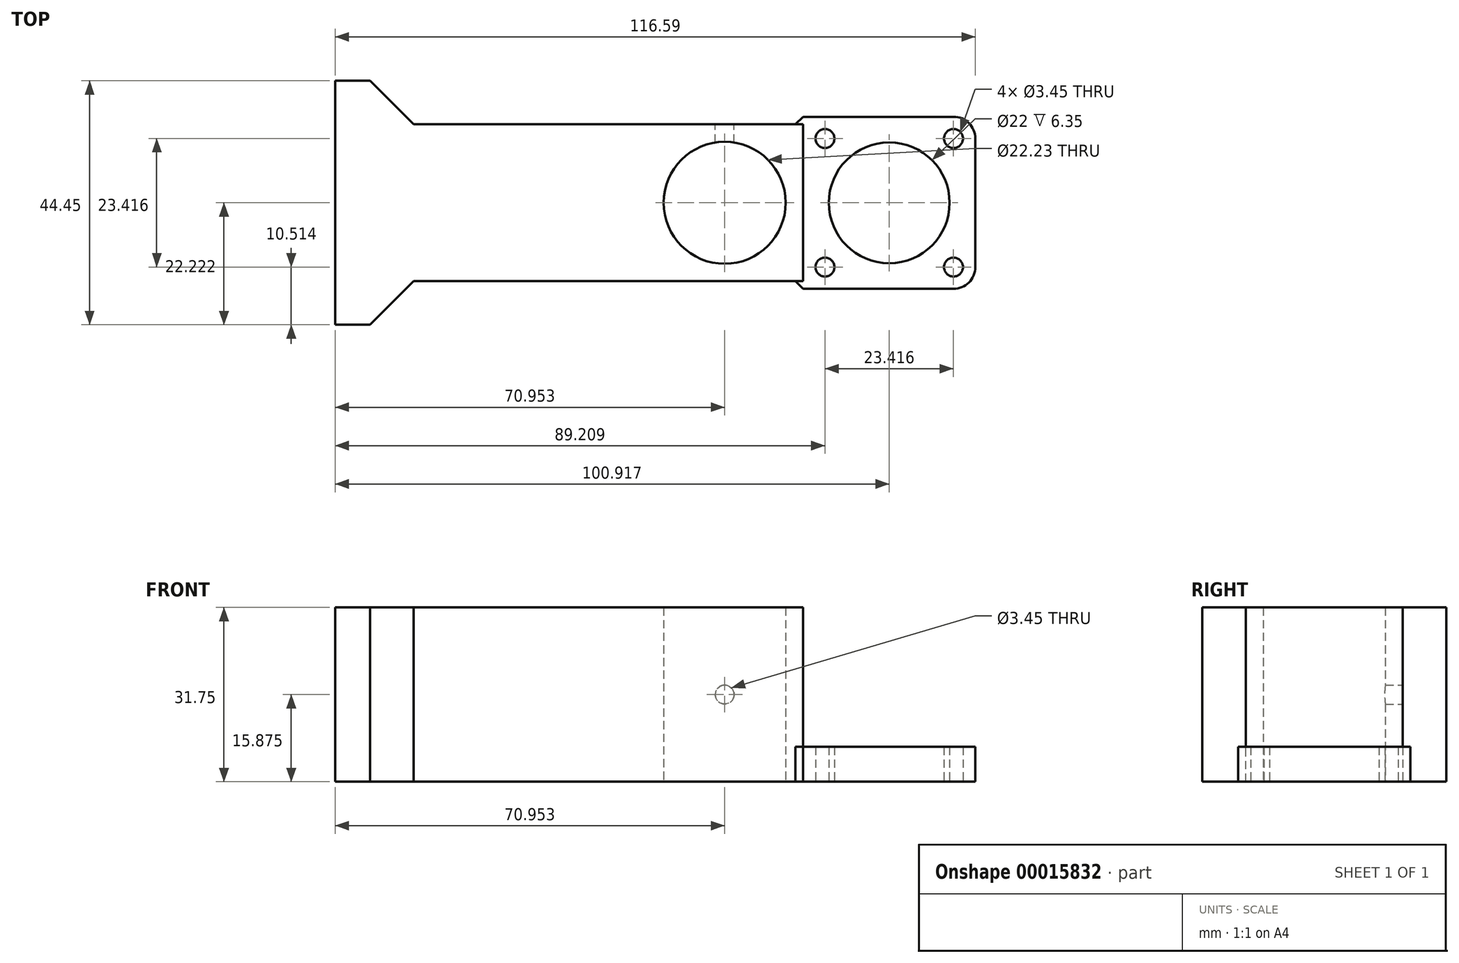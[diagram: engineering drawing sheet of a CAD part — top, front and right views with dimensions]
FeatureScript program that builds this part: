
annotation { "Feature Type Name" : "Feature", "Feature Type Description" : "" }
export const myFeature = defineFeature(function(context is Context, id is Id, definition is map)
    precondition{}
    {
        {
            var Q0;
            Q0=qCreatedBy(makeId("Top.planeOp"),FACE);
            var sketch = newSketch(context, id + "F0", { "sketchPlane" : qUnion([Q0])});
            skLineSegment(sketch, "E0.bottom", {"start": v(0, 0) * mm, "end": v(-78.9, 0) * mm});
            skLineSegment(sketch, "E0.top", {"start": v(0, -28.58) * mm, "end": v(-78.9, -28.58) * mm});
            skCircle(sketch, "E1", {"center": v(-14.29, -14.29) * mm, "radius": 11.11 * mm});
            skLineSegment(sketch, "E2", {"start": v(-14.29, -14.29) * mm, "end": v(-85.24, -14.29) * mm});
            skLineSegment(sketch, "E3.bottom", {"start": v(-78.9, -28.58) * mm, "end": v(-85.24, -28.58) * mm, "construction": true});
            skLineSegment(sketch, "E3.top", {"start": v(-78.9, -36.51) * mm, "end": v(-85.24, -36.51) * mm});
            skLineSegment(sketch, "E3.left", {"start": v(-78.9, -28.58) * mm, "end": v(-78.9, -36.51) * mm});
            skLineSegment(sketch, "E3.right", {"start": v(-85.24, -28.58) * mm, "end": v(-85.24, -36.51) * mm});
            skLineSegment(sketch, "E4.bottom", {"start": v(-78.9, 0) * mm, "end": v(-85.24, 0) * mm, "construction": true});
            skLineSegment(sketch, "E4.top", {"start": v(-78.9, 7.94) * mm, "end": v(-85.24, 7.94) * mm});
            skLineSegment(sketch, "E4.left", {"start": v(-78.9, 0) * mm, "end": v(-78.9, 7.94) * mm});
            skLineSegment(sketch, "E4.right", {"start": v(-85.24, 0) * mm, "end": v(-85.24, 7.94) * mm});
            skLineSegment(sketch, "E5", {"start": v(-85.24, 0) * mm, "end": v(-85.24, -28.58) * mm});
            skLineSegment(sketch, "E6.rect.bottom", {"start": v(31.35, -29.96) * mm, "end": v(0, -29.96) * mm});
            skLineSegment(sketch, "E6.rect.top", {"start": v(31.35, 1.39) * mm, "end": v(0, 1.39) * mm});
            skLineSegment(sketch, "E6.rect.left", {"start": v(31.35, -29.96) * mm, "end": v(31.35, 1.39) * mm});
            skPoint(sketch, "E6.rect.middle", {"position": v(15.68, -14.29) * mm});
            skLineSegment(sketch, "E7", {"start": v(0, 1.39) * mm, "end": v(0, 0) * mm});
            skLineSegment(sketch, "E8", {"start": v(0, 0) * mm, "end": v(0, -28.58) * mm, "construction": true});
            skLineSegment(sketch, "E9", {"start": v(0, -28.58) * mm, "end": v(0, -29.96) * mm});
            skLineSegment(sketch, "E10", {"start": v(-14.29, -14.29) * mm, "end": v(0, -14.29) * mm});
            skLineSegment(sketch, "E11.rect.bottom", {"start": v(27.38, -26) * mm, "end": v(3.97, -26) * mm, "construction": true});
            skLineSegment(sketch, "E11.rect.top", {"start": v(27.38, -2.58) * mm, "end": v(3.97, -2.58) * mm, "construction": true});
            skLineSegment(sketch, "E11.rect.left", {"start": v(27.38, -26) * mm, "end": v(27.38, -2.58) * mm, "construction": true});
            skLineSegment(sketch, "E11.rect.right", {"start": v(3.97, -26) * mm, "end": v(3.97, -2.58) * mm, "construction": true});
            skCircle(sketch, "E12", {"center": v(27.38, -26) * mm, "radius": 3.97 * mm, "construction": true});
            skCircle(sketch, "E13", {"center": v(27.38, -2.58) * mm, "radius": 1.73 * mm});
            skCircle(sketch, "E14", {"center": v(3.97, -2.58) * mm, "radius": 1.73 * mm});
            skCircle(sketch, "E15", {"center": v(3.97, -26) * mm, "radius": 1.73 * mm});
            skCircle(sketch, "E16", {"center": v(27.38, -26) * mm, "radius": 1.73 * mm});
            skCircle(sketch, "E17", {"center": v(15.68, -14.29) * mm, "radius": 11 * mm});
            skSolve(sketch);
        }
        {
            var Q0;
            Q0=qSketchRegion(id+"F0",true);
            extrude(context, id + "F1", {"entities" : qUnion([Q0]), "depth" : 31.75 * mm});
        }
        {
            var Q0;
            Q0=makeQuery(id+"F1.opExtrude","SWEPT_EDGE",EDGE,{"disambiguationData":[OSD([sQuery(id+"F0.wireOp",EDGE,"E0.bottom"),sQuery(id+"F0.wireOp",EDGE,"E4.left")])]});
            var Q1;
            Q1=makeQuery(id+"F1.opExtrude","SWEPT_EDGE",EDGE,{"disambiguationData":[OSD([sQuery(id+"F0.wireOp",EDGE,"E0.top"),sQuery(id+"F0.wireOp",EDGE,"E3.left")])]});
            chamfer(context, id + "F2", {"entities" : qUnion([Q0, Q1]), "width" : 7.94 * mm, "tangentPropagation" : true});
        }
        {
            var Q0;
            Q0=makeQuery(id+"F1.opExtrude","CAP_FACE",FACE,{"disambiguationData":[OSD([sQuery(id+"F0.wireOp",EDGE,"E0.bottom"),sQuery(id+"F0.wireOp",EDGE,"E0.top"),sQuery(id+"F0.wireOp",EDGE,"E1"),sQuery(id+"F0.wireOp",EDGE,"E3.top"),sQuery(id+"F0.wireOp",EDGE,"E3.left"),sQuery(id+"F0.wireOp",EDGE,"E3.right"),sQuery(id+"F0.wireOp",EDGE,"E4.top"),sQuery(id+"F0.wireOp",EDGE,"E4.left"),sQuery(id+"F0.wireOp",EDGE,"E4.right"),sQuery(id+"F0.wireOp",EDGE,"E5"),sQuery(id+"F0.wireOp",EDGE,"E6.rect.bottom"),sQuery(id+"F0.wireOp",EDGE,"E6.rect.top"),sQuery(id+"F0.wireOp",EDGE,"E6.rect.left"),sQuery(id+"F0.wireOp",EDGE,"E7"),sQuery(id+"F0.wireOp",EDGE,"E9"),sQuery(id+"F0.wireOp",EDGE,"E13"),sQuery(id+"F0.wireOp",EDGE,"E14"),sQuery(id+"F0.wireOp",EDGE,"E15"),sQuery(id+"F0.wireOp",EDGE,"E16"),sQuery(id+"F0.wireOp",EDGE,"E17")])],"isStart":false});
            var sketch = newSketch(context, id + "F3", { "sketchPlane" : qUnion([Q0])});
            skLineSegment(sketch, "E18.rect.bottom", {"start": v(0, 1.39) * mm, "end": v(31.35, 1.39) * mm});
            skLineSegment(sketch, "E18.rect.top", {"start": v(0, -29.96) * mm, "end": v(31.35, -29.96) * mm});
            skLineSegment(sketch, "E18.rect.left", {"start": v(0, 1.39) * mm, "end": v(0, -29.96) * mm});
            skLineSegment(sketch, "E18.rect.right", {"start": v(31.35, 1.39) * mm, "end": v(31.35, -29.96) * mm});
            skPoint(sketch, "E18.rect.middle", {"position": v(15.68, -14.29) * mm});
            skSolve(sketch);
        }
        {
            var Q0;
            Q0 = qSketchRegion(id + "F3", true);
            extrude(context, id + "F4", {"entities" : qUnion([Q0]), "operationType" : NewBodyOperationType.REMOVE, "oppositeDirection" : true, "depth" : 25.4 * mm});
        }
        {
            var Q0;
            Q0=makeQuery(id+"F1.opExtrude","SWEPT_FACE",FACE,{"disambiguationData":[OSD([sQuery(id+"F0.wireOp",EDGE,"E0.bottom")])]});
            var sketch = newSketch(context, id + "F5", { "sketchPlane" : qUnion([Q0])});
            skLineSegment(sketch, "E19", {"start": v(14.29, 31.75) * mm, "end": v(14.29, 0) * mm});
            skCircle(sketch, "E20", {"center": v(14.29, 15.88) * mm, "radius": 1.73 * mm});
            skSolve(sketch);
        }
        {
            var Q0;
            Q0 = qSketchRegion(id + "F5", true);
            var Q1;
            Q1=makeQuery(id+"F1.opExtrude","SWEPT_FACE",FACE,{"disambiguationData":[OSD([sQuery(id+"F0.wireOp",EDGE,"E1")])]});
            extrude(context, id + "F6", {"entities" : qUnion([Q0]), "operationType" : NewBodyOperationType.REMOVE, "endBound" : BoundingType.UP_TO_SURFACE, "oppositeDirection" : true, "endBoundEntityFace" : qUnion([Q1]), "depth" : 25.4 * mm});
        }
        {
            var Q0;
            Q0=makeQuery(id+"F1.opExtrude","SWEPT_EDGE",EDGE,{"disambiguationData":[OSD([sQuery(id+"F0.wireOp",EDGE,"E6.rect.bottom"),sQuery(id+"F0.wireOp",EDGE,"E6.rect.left")])]});
            var Q1;
            Q1=makeQuery(id+"F1.opExtrude","SWEPT_EDGE",EDGE,{"disambiguationData":[OSD([sQuery(id+"F0.wireOp",EDGE,"E6.rect.top"),sQuery(id+"F0.wireOp",EDGE,"E6.rect.left")])]});
            fillet(context, id + "F7", {"entities" : qUnion([Q0, Q1]), "radius" : 3.97 * mm, "tangentPropagation" : true, "allowEdgeOverflow" : false});
        }
        {
            var Q0;
            {var subQ1=sQuery(id+"F0.wireOp",EDGE,"E7");var subQ2=sQuery(id+"F0.wireOp",EDGE,"E0.bottom");Q0=makeQuery(id+"F4.boolean.opBoolean","SPLIT",EDGE,{"disambiguationData":[TD([makeQuery(id+"F1.opExtrude","CAP_FACE",FACE,{"disambiguationData":[OSD([subQ2,sQuery(id+"F0.wireOp",EDGE,"E0.top"),sQuery(id+"F0.wireOp",EDGE,"E1"),sQuery(id+"F0.wireOp",EDGE,"E3.top"),sQuery(id+"F0.wireOp",EDGE,"E3.left"),sQuery(id+"F0.wireOp",EDGE,"E3.right"),sQuery(id+"F0.wireOp",EDGE,"E4.top"),sQuery(id+"F0.wireOp",EDGE,"E4.left"),sQuery(id+"F0.wireOp",EDGE,"E4.right"),sQuery(id+"F0.wireOp",EDGE,"E5"),sQuery(id+"F0.wireOp",EDGE,"E6.rect.bottom"),sQuery(id+"F0.wireOp",EDGE,"E6.rect.top"),sQuery(id+"F0.wireOp",EDGE,"E6.rect.left"),subQ1,sQuery(id+"F0.wireOp",EDGE,"E9"),sQuery(id+"F0.wireOp",EDGE,"E13"),sQuery(id+"F0.wireOp",EDGE,"E14"),sQuery(id+"F0.wireOp",EDGE,"E15"),sQuery(id+"F0.wireOp",EDGE,"E16"),sQuery(id+"F0.wireOp",EDGE,"E17")])],"isStart":true})])],"derivedFrom":makeQuery(id+"F1.opExtrude","SWEPT_EDGE",EDGE,{"disambiguationData":[OSD([subQ2,subQ1])]})});}
            var Q1;
            {var subQ1=sQuery(id+"F0.wireOp",EDGE,"E0.top");var subQ2=sQuery(id+"F0.wireOp",EDGE,"E9");Q1=makeQuery(id+"F4.boolean.opBoolean","SPLIT",EDGE,{"disambiguationData":[TD([makeQuery(id+"F1.opExtrude","CAP_FACE",FACE,{"disambiguationData":[OSD([sQuery(id+"F0.wireOp",EDGE,"E0.bottom"),subQ1,sQuery(id+"F0.wireOp",EDGE,"E1"),sQuery(id+"F0.wireOp",EDGE,"E3.top"),sQuery(id+"F0.wireOp",EDGE,"E3.left"),sQuery(id+"F0.wireOp",EDGE,"E3.right"),sQuery(id+"F0.wireOp",EDGE,"E4.top"),sQuery(id+"F0.wireOp",EDGE,"E4.left"),sQuery(id+"F0.wireOp",EDGE,"E4.right"),sQuery(id+"F0.wireOp",EDGE,"E5"),sQuery(id+"F0.wireOp",EDGE,"E6.rect.bottom"),sQuery(id+"F0.wireOp",EDGE,"E6.rect.top"),sQuery(id+"F0.wireOp",EDGE,"E6.rect.left"),sQuery(id+"F0.wireOp",EDGE,"E7"),subQ2,sQuery(id+"F0.wireOp",EDGE,"E13"),sQuery(id+"F0.wireOp",EDGE,"E14"),sQuery(id+"F0.wireOp",EDGE,"E15"),sQuery(id+"F0.wireOp",EDGE,"E16"),sQuery(id+"F0.wireOp",EDGE,"E17")])],"isStart":true})])],"derivedFrom":makeQuery(id+"F1.opExtrude","SWEPT_EDGE",EDGE,{"disambiguationData":[OSD([subQ1,subQ2])]})});}
            chamfer(context, id + "F8", {"entities" : qUnion([Q0, Q1]), "width" : 1.39 * mm, "tangentPropagation" : true});
        }
    });
